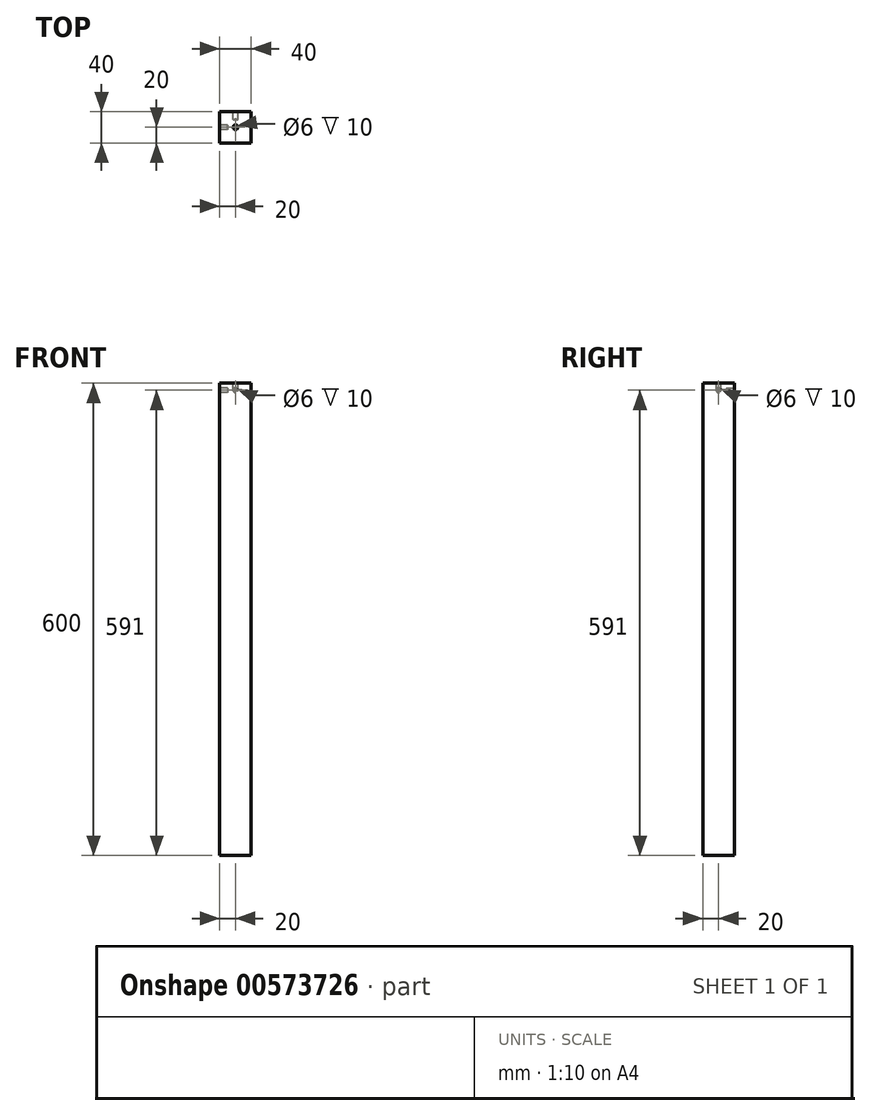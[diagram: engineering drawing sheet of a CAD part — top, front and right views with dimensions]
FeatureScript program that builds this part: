
annotation { "Feature Type Name" : "Feature", "Feature Type Description" : "" }
export const myFeature = defineFeature(function(context is Context, id is Id, definition is map)
    precondition{}
    {
        {
            var Q0;
            Q0=qCreatedBy(makeId("Top.planeOp"),FACE);
            var sketch = newSketch(context, id + "F0", { "sketchPlane" : qUnion([Q0])});
            skLineSegment(sketch, "E0.bottom", {"start": v(0, 0) * mm, "end": v(40, 0) * mm});
            skLineSegment(sketch, "E0.top", {"start": v(0, 40) * mm, "end": v(40, 40) * mm});
            skLineSegment(sketch, "E0.left", {"start": v(0, 0) * mm, "end": v(0, 40) * mm});
            skLineSegment(sketch, "E0.right", {"start": v(40, 0) * mm, "end": v(40, 40) * mm});
            skSolve(sketch);
        }
        {
            var Q0;
            Q0=makeQuery(id+"F0.imprint","IMPRINT",FACE,{"disambiguationData":[TD([[makeQuery(id+"F0.imprint","IMPRINT",EDGE,{"derivedFrom":sQuery(id+"F0.wireOp",EDGE,"E0.bottom")}),1.0]])]});
            extrude(context, id + "F1", {"entities" : qUnion([Q0]), "depth" : 600 * mm, "offsetDistance" : 25 * mm});
        }
        {
            var Q0;
            Q0=makeQuery(id+"F1.opExtrude","SWEPT_FACE",FACE,{"disambiguationData":[OSD([sQuery(id+"F0.wireOp",EDGE,"E0.top")])]});
            var sketch = newSketch(context, id + "F2", { "sketchPlane" : qUnion([Q0])});
            skCircle(sketch, "E1", {"center": v(-20, 591) * mm, "radius": 3 * mm});
            skSolve(sketch);
        }
        {
            var Q0;
            Q0 = qSketchRegion(id + "F2", true);
            extrude(context, id + "F3", {"entities" : qUnion([Q0]), "operationType" : NewBodyOperationType.REMOVE, "oppositeDirection" : true, "depth" : 10 * mm, "offsetDistance" : 25 * mm});
        }
        {
            var Q0;
            Q0=makeQuery(id+"F1.opExtrude","SWEPT_FACE",FACE,{"disambiguationData":[OSD([sQuery(id+"F0.wireOp",EDGE,"E0.left")])]});
            var sketch = newSketch(context, id + "F4", { "sketchPlane" : qUnion([Q0])});
            skCircle(sketch, "E2", {"center": v(-20, 591) * mm, "radius": 3 * mm});
            skSolve(sketch);
        }
        {
            var Q0;
            Q0 = qSketchRegion(id + "F4", true);
            extrude(context, id + "F5", {"entities" : qUnion([Q0]), "operationType" : NewBodyOperationType.REMOVE, "oppositeDirection" : true, "depth" : 10 * mm, "offsetDistance" : 25 * mm});
        }
        {
            var Q0;
            Q0=makeQuery(id+"F1.opExtrude","CAP_FACE",FACE,{"disambiguationData":[OSD([sQuery(id+"F0.wireOp",EDGE,"E0.bottom"),sQuery(id+"F0.wireOp",EDGE,"E0.top"),sQuery(id+"F0.wireOp",EDGE,"E0.left"),sQuery(id+"F0.wireOp",EDGE,"E0.right")])],"isStart":false});
            var sketch = newSketch(context, id + "F6", { "sketchPlane" : qUnion([Q0])});
            skCircle(sketch, "E3", {"center": v(20, 20) * mm, "radius": 3 * mm});
            skSolve(sketch);
        }
        {
            var Q0;
            Q0 = qSketchRegion(id + "F6", true);
            extrude(context, id + "F7", {"entities" : qUnion([Q0]), "operationType" : NewBodyOperationType.REMOVE, "oppositeDirection" : true, "depth" : 10 * mm, "offsetDistance" : 25 * mm});
        }
    });
